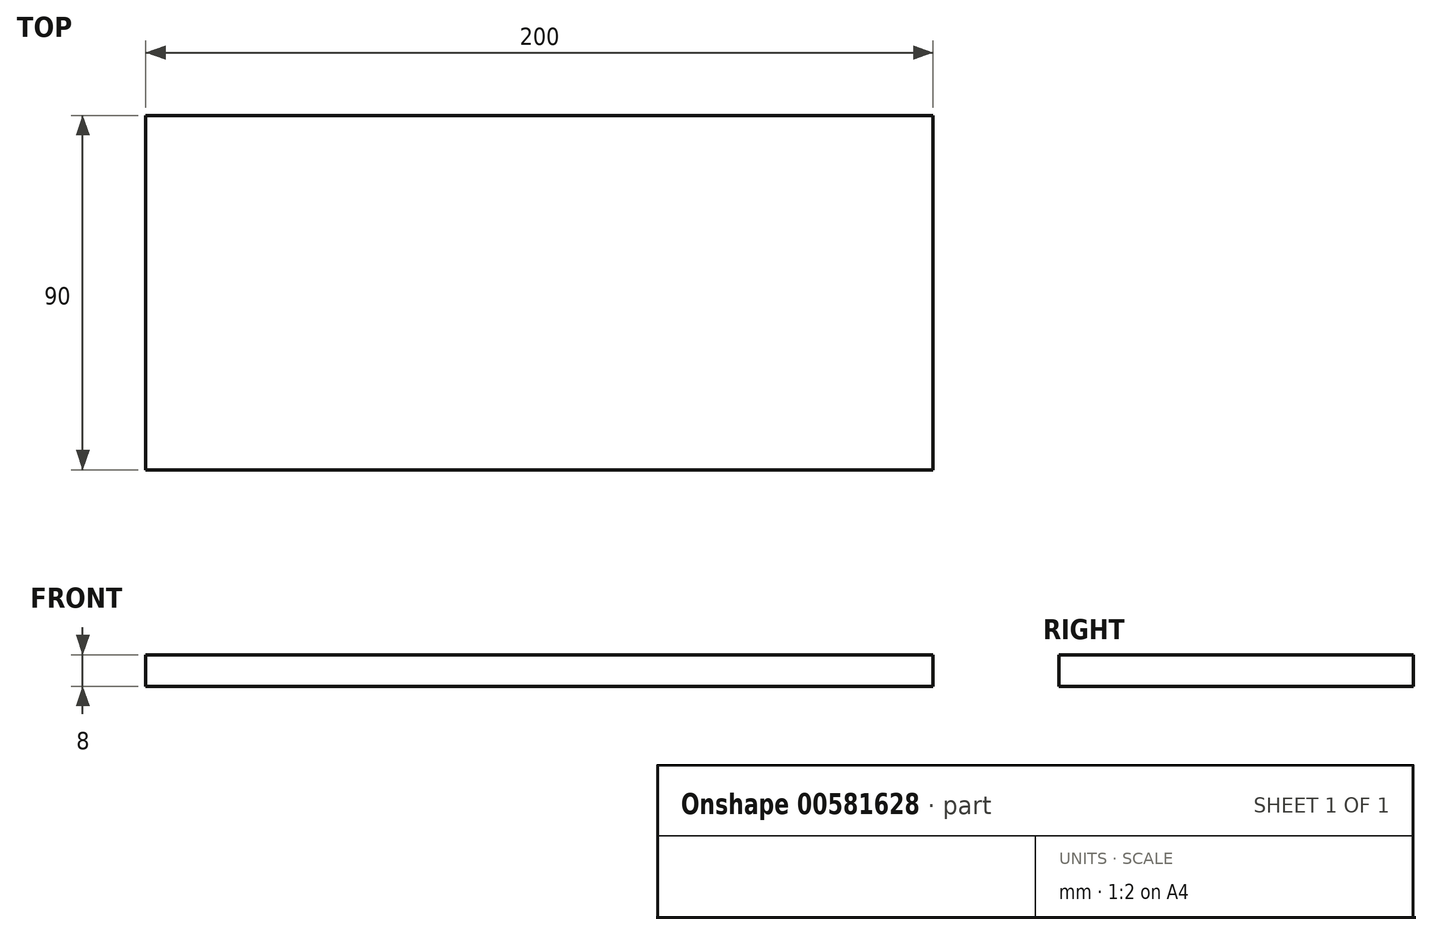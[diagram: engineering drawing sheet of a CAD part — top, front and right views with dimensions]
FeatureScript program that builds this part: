
annotation { "Feature Type Name" : "Feature", "Feature Type Description" : "" }
export const myFeature = defineFeature(function(context is Context, id is Id, definition is map)
    precondition{}
    {
        {
            var Q0;
            Q0=qCreatedBy(makeId("Top.planeOp"),FACE);
            var sketch = newSketch(context, id + "F0", { "sketchPlane" : qUnion([Q0])});
            skLineSegment(sketch, "E0.bottom", {"start": v(100, -45) * mm, "end": v(-100, -45) * mm});
            skLineSegment(sketch, "E0.top", {"start": v(100, 45) * mm, "end": v(-100, 45) * mm});
            skLineSegment(sketch, "E0.left", {"start": v(100, -45) * mm, "end": v(100, 45) * mm});
            skLineSegment(sketch, "E0.right", {"start": v(-100, -45) * mm, "end": v(-100, 45) * mm});
            skPoint(sketch, "E0.middle", {"position": v(0, 0) * mm});
            skSolve(sketch);
        }
        {
            var Q0;
            Q0 = qSketchRegion(id + "F0", true);
            extrude(context, id + "F1", {"entities" : qUnion([Q0]), "endBound" : BoundingType.SYMMETRIC, "depth" : 8 * mm, "offsetDistance" : 25 * mm});
        }
    });
